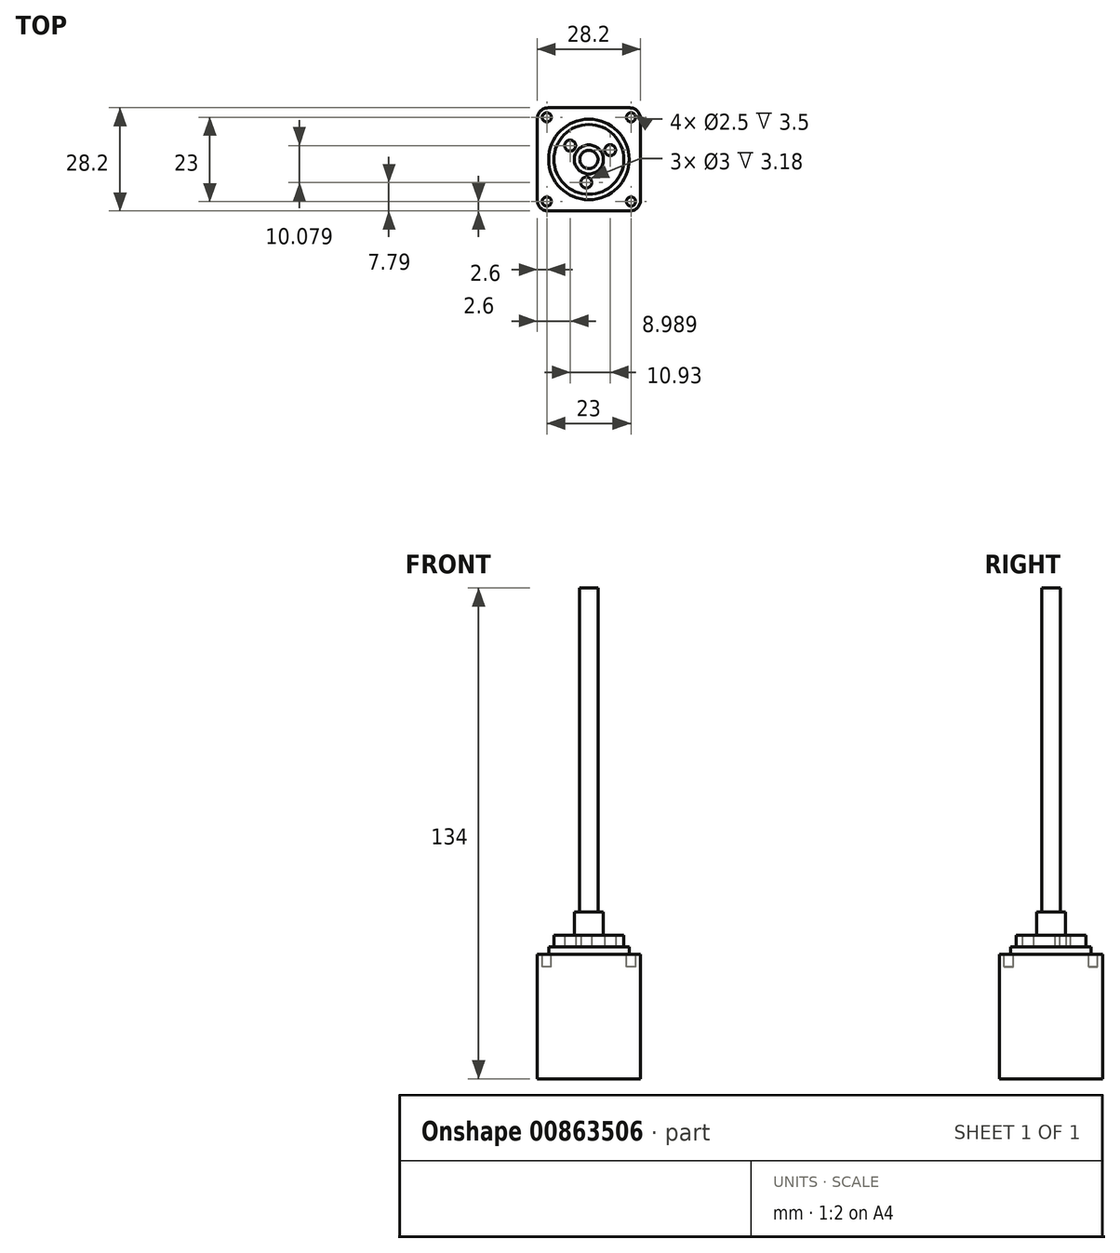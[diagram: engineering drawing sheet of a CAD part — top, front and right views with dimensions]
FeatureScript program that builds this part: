
annotation { "Feature Type Name" : "Feature", "Feature Type Description" : "" }
export const myFeature = defineFeature(function(context is Context, id is Id, definition is map)
    precondition{}
    {
        {
            var Q0;
            Q0=qCreatedBy(makeId("Front.planeOp"),FACE);
            var sketch = newSketch(context, id + "F0", { "sketchPlane" : qUnion([Q0])});
            skLineSegment(sketch, "E0.bottom", {"start": v(-14.1, 0) * mm, "end": v(14.1, 0) * mm});
            skLineSegment(sketch, "E0.top", {"start": v(-14.1, -34) * mm, "end": v(14.1, -34) * mm});
            skLineSegment(sketch, "E0.left", {"start": v(-14.1, 0) * mm, "end": v(-14.1, -34) * mm});
            skLineSegment(sketch, "E0.right", {"start": v(14.1, 0) * mm, "end": v(14.1, -34) * mm});
            skLineSegment(sketch, "E1", {"start": v(0, 54.6) * mm, "end": v(0, -51.08) * mm, "construction": true});
            skSolve(sketch);
        }
        {
            var Q0;
            Q0=makeQuery(id+"F0.imprint","IMPRINT",FACE,{"disambiguationData":[TD([[makeQuery(id+"F0.imprint","IMPRINT",EDGE,{"derivedFrom":sQuery(id+"F0.wireOp",EDGE,"E0.bottom")}),-1.0]])]});
            extrude(context, id + "F1", {"entities" : qUnion([Q0]), "offsetDistance" : 25 * mm, "depth" : 28.2 * mm, "symmetric" : true});
        }
        {
            var Q0;
            Q0=makeQuery(id+"F1.opExtrude","SWEPT_FACE",FACE,{"disambiguationData":[OSD([sQuery(id+"F0.wireOp",EDGE,"E0.bottom")])]});
            var sketch = newSketch(context, id + "F2", { "sketchPlane" : qUnion([Q0])});
            skLineSegment(sketch, "E2", {"start": v(-22.05, 0) * mm, "end": v(28.17, 0) * mm, "construction": true});
            skLineSegment(sketch, "E3", {"start": v(0, 17.29) * mm, "end": v(0, -17.48) * mm, "construction": true});
            skCircle(sketch, "E4", {"center": v(11.5, 11.5) * mm, "radius": 1.25 * mm});
            skPoint(sketch, "E5", {"position": v(0, 14.1) * mm});
            skCircle(sketch, "E6.MirrorC", {"center": v(11.5, -11.5) * mm, "radius": 1.25 * mm});
            skCircle(sketch, "E7.MirrorC", {"center": v(-11.5, -11.5) * mm, "radius": 1.25 * mm});
            skCircle(sketch, "E8.MirrorC", {"center": v(-11.5, 11.5) * mm, "radius": 1.25 * mm});
            skSolve(sketch);
        }
        {
            var Q0;
            Q0=qSketchRegion(id+"F2",true);
            extrude(context, id + "F3", {"entities" : qUnion([Q0]), "operationType" : NewBodyOperationType.REMOVE, "oppositeDirection" : true, "depth" : 3.5 * mm});
        }
        {
            var Q0;
            Q0=makeQuery(id+"F1.opExtrude","SWEPT_FACE",FACE,{"disambiguationData":[OSD([sQuery(id+"F0.wireOp",EDGE,"E0.bottom")])]});
            var sketch = newSketch(context, id + "F4", { "sketchPlane" : qUnion([Q0])});
            skCircle(sketch, "E9", {"center": v(0, 0) * mm, "radius": 11 * mm});
            skSolve(sketch);
        }
        {
            var Q0;
            Q0=qSketchRegion(id+"F4",true);
            extrude(context, id + "F5", {"entities" : qUnion([Q0]), "operationType" : NewBodyOperationType.ADD, "depth" : 2 * mm});
        }
        {
            var Q0;
            Q0=makeQuery(id+"F1.opExtrude","SWEPT_FACE",FACE,{"disambiguationData":[OSD([sQuery(id+"F0.wireOp",EDGE,"E0.bottom")])]});
            var sketch = newSketch(context, id + "F6", { "sketchPlane" : qUnion([Q0])});
            skCircle(sketch, "E10", {"center": v(0, 0) * mm, "radius": 2.5 * mm});
            skSolve(sketch);
        }
        {
            var Q0;
            Q0=qSketchRegion(id+"F6",true);
            extrude(context, id + "F7", {"entities" : qUnion([Q0]), "depth" : 100 * mm});
        }
        {
            var Q0;
            Q0=makeQuery(id+"F1.opExtrude","CAP_EDGE",EDGE,{"disambiguationData":[OSD([sQuery(id+"F0.wireOp",EDGE,"E0.left")])],"isStart":true});
            var Q1;
            Q1=makeQuery(id+"F1.opExtrude","CAP_EDGE",EDGE,{"disambiguationData":[OSD([sQuery(id+"F0.wireOp",EDGE,"E0.right")])],"isStart":true});
            var Q2;
            Q2=makeQuery(id+"F1.opExtrude","CAP_EDGE",EDGE,{"disambiguationData":[OSD([sQuery(id+"F0.wireOp",EDGE,"E0.left")])],"isStart":false});
            var Q3;
            Q3=makeQuery(id+"F1.opExtrude","CAP_EDGE",EDGE,{"disambiguationData":[OSD([sQuery(id+"F0.wireOp",EDGE,"E0.right")])],"isStart":false});
            fillet(context, id + "F8", {"entities" : qUnion([Q0, Q1, Q2, Q3]), "radius" : 3 * mm, "tangentPropagation" : true, "allowEdgeOverflow" : false});
        }
        {
            var Q0;
            Q0=makeQuery(id+"F5.opExtrude","CAP_FACE",FACE,{"disambiguationData":[OSD([sQuery(id+"F4.wireOp",EDGE,"E9")])],"isStart":false});
            var sketch = newSketch(context, id + "F9", { "sketchPlane" : qUnion([Q0])});
            skCircle(sketch, "E11", {"center": v(0, 0) * mm, "radius": 9.53 * mm});
            skCircle(sketch, "E12", {"center": v(0, 0) * mm, "radius": 2.5 * mm});
            skSolve(sketch);
        }
        {
            var Q0;
            Q0=qSketchRegion(id+"F9",true);
            extrude(context, id + "F10", {"entities" : qUnion([Q0]), "depth" : 3.18 * mm});
        }
        {
            var Q0;
            Q0=makeQuery(id+"F5.opExtrude","CAP_FACE",FACE,{"disambiguationData":[OSD([sQuery(id+"F4.wireOp",EDGE,"E9")])],"isStart":false});
            var sketch = newSketch(context, id + "F11", { "sketchPlane" : qUnion([Q0])});
            skCircle(sketch, "E13", {"center": v(0, 0) * mm, "radius": 3.97 * mm});
            skCircle(sketch, "E14", {"center": v(0, 0) * mm, "radius": 2.5 * mm});
            skSolve(sketch);
        }
        {
            var Q0;
            Q0=makeQuery(id+"F11.imprint","IMPRINT",FACE,{"disambiguationData":[TD([[makeQuery(id+"F11.imprint","IMPRINT",EDGE,{"derivedFrom":sQuery(id+"F11.wireOp",EDGE,"E13")}),1.0]])]});
            extrude(context, id + "F12", {"entities" : qUnion([Q0]), "operationType" : NewBodyOperationType.ADD, "depth" : 9.53 * mm});
        }
        {
            var Q0;
            Q0=makeQuery(id+"F5.opExtrude","CAP_FACE",FACE,{"disambiguationData":[OSD([sQuery(id+"F4.wireOp",EDGE,"E9")])],"isStart":false});
            var sketch = newSketch(context, id + "F13", { "sketchPlane" : qUnion([Q0])});
            skCircle(sketch, "E15", {"center": v(5.82, 2.54) * mm, "radius": 1.5 * mm});
            skCircle(sketch, "E16", {"center": v(0, 0) * mm, "radius": 6.35 * mm, "construction": true});
            skCircle(sketch, "E17.1.0", {"center": v(-5.11, 3.77) * mm, "radius": 1.5 * mm});
            skCircle(sketch, "E17.2.0", {"center": v(-0.7, -6.31) * mm, "radius": 1.5 * mm});
            skSolve(sketch);
        }
        {
            var Q0;
            Q0=qSketchRegion(id+"F13",true);
            extrude(context, id + "F14", {"entities" : qUnion([Q0]), "operationType" : NewBodyOperationType.REMOVE, "endBound" : BoundingType.UP_TO_NEXT, "depth" : 25 * mm});
        }
    });
